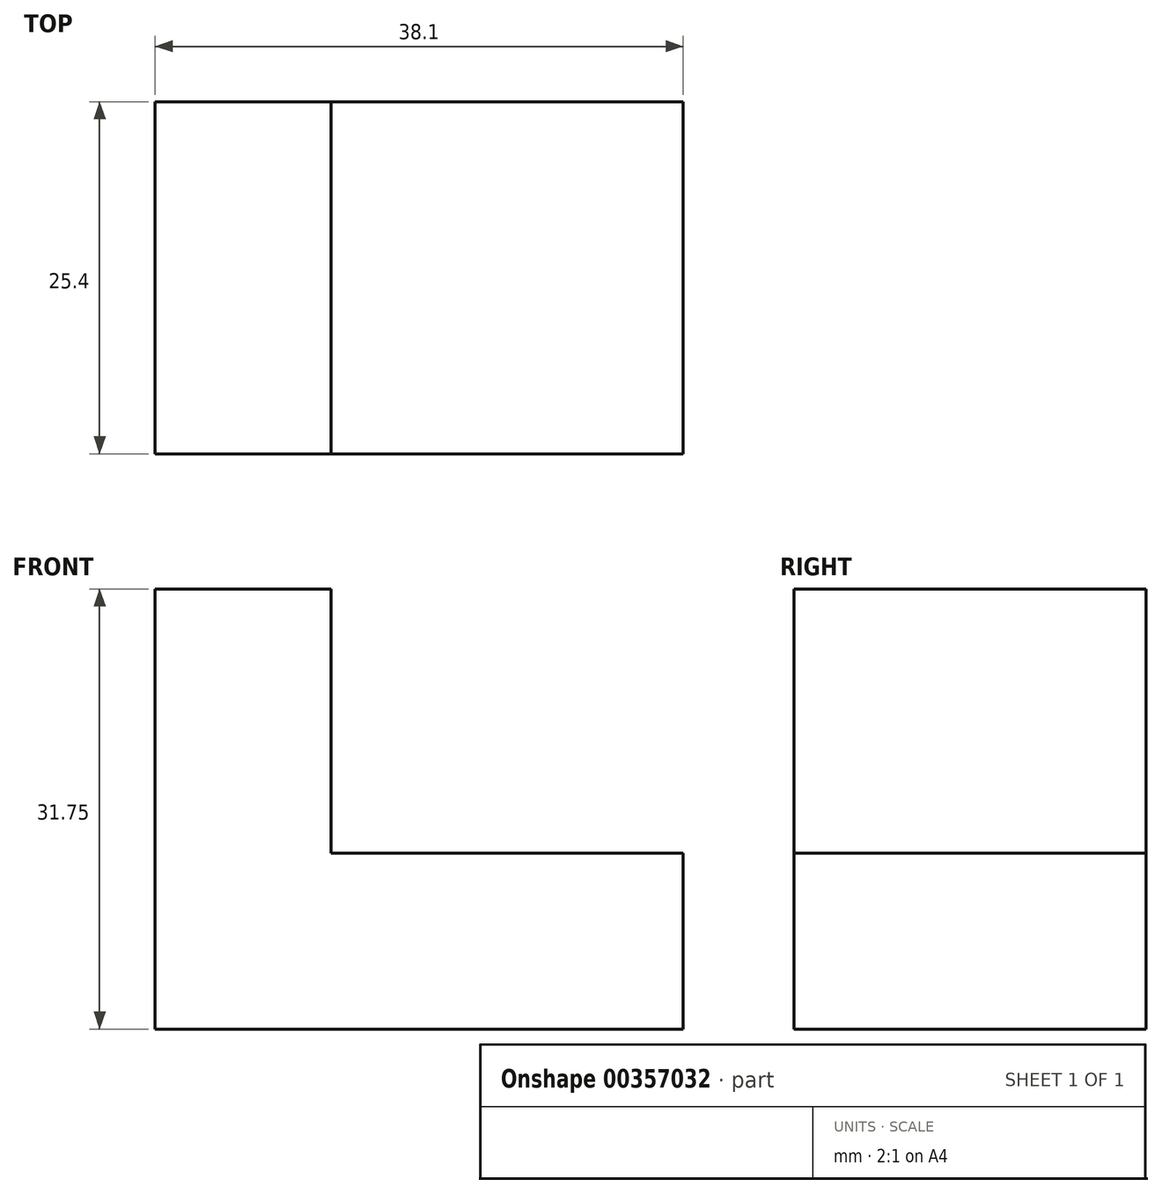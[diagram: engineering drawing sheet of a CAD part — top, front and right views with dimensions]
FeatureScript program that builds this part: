
annotation { "Feature Type Name" : "Feature", "Feature Type Description" : "" }
export const myFeature = defineFeature(function(context is Context, id is Id, definition is map)
    precondition{}
    {
        {
            var Q0;
            Q0=qCreatedBy(makeId("Front.planeOp"),FACE);
            var sketch = newSketch(context, id + "F0", { "sketchPlane" : qUnion([Q0])});
            skLineSegment(sketch, "E0", {"start": v(38.1, 0) * mm, "end": v(38.1, 12.7) * mm});
            skLineSegment(sketch, "E1", {"start": v(38.1, 12.7) * mm, "end": v(12.7, 12.7) * mm});
            skLineSegment(sketch, "E2", {"start": v(12.7, 12.7) * mm, "end": v(12.7, 31.75) * mm});
            skLineSegment(sketch, "E3", {"start": v(12.7, 31.75) * mm, "end": v(0, 31.75) * mm});
            skLineSegment(sketch, "E4", {"start": v(0, 31.75) * mm, "end": v(0, 0) * mm});
            skLineSegment(sketch, "E5", {"start": v(0, 0) * mm, "end": v(38.1, 0) * mm});
            skSolve(sketch);
        }
        {
            var Q0;
            Q0 = qSketchRegion(id + "F0", true);
            extrude(context, id + "F1", {"entities" : qUnion([Q0]), "depth" : 25.4 * mm});
        }
    });
